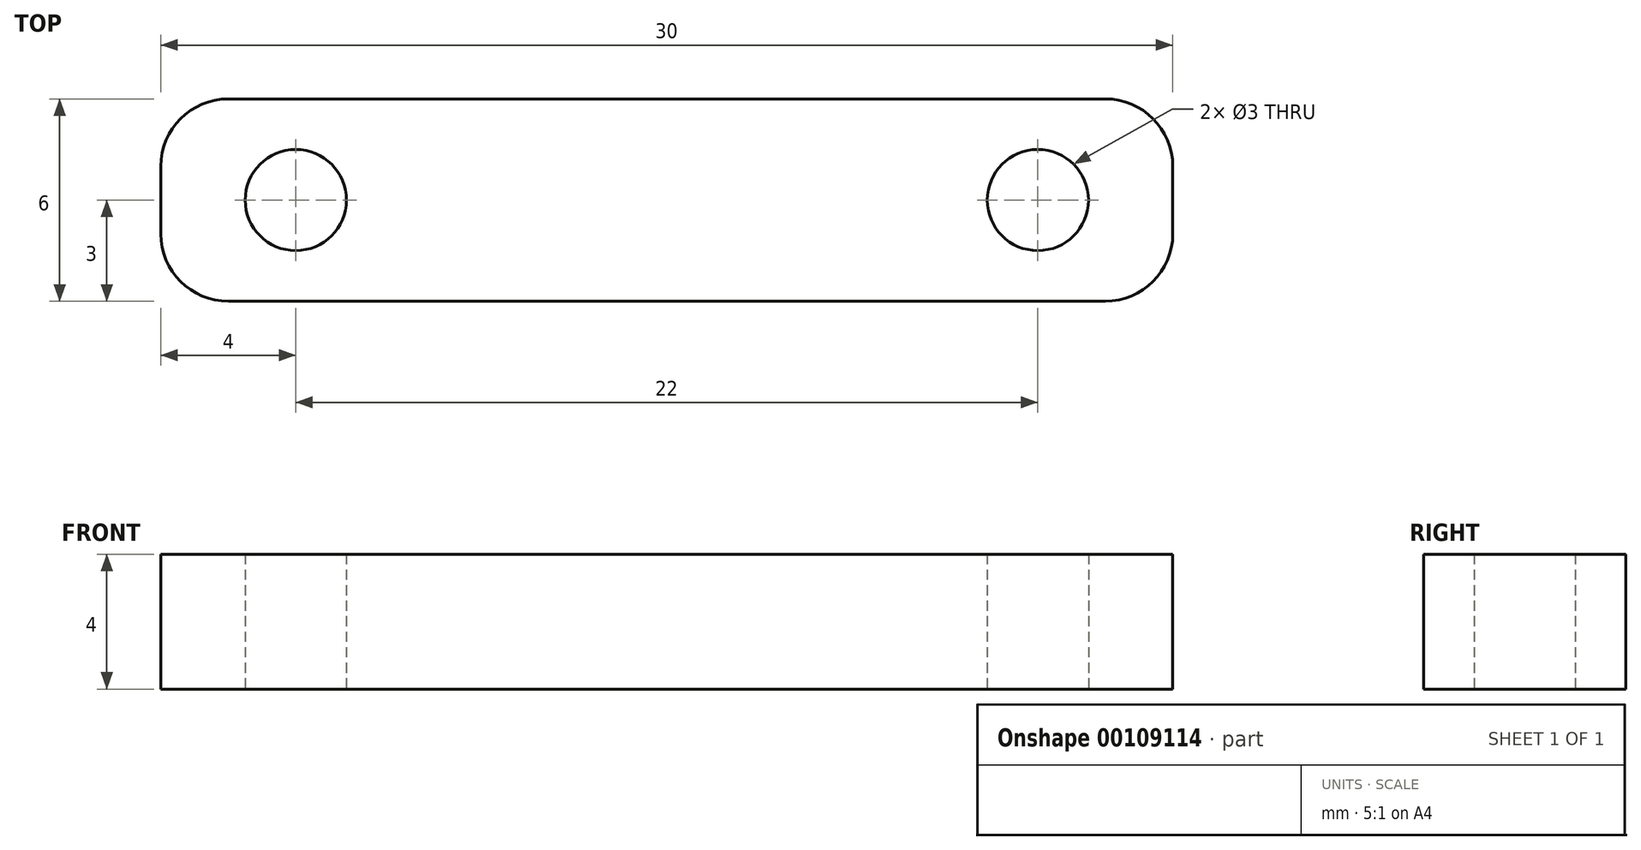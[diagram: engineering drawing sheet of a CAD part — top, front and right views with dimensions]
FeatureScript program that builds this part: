
annotation { "Feature Type Name" : "Feature", "Feature Type Description" : "" }
export const myFeature = defineFeature(function(context is Context, id is Id, definition is map)
    precondition{}
    {
        {
            var Q0;
            Q0=qCreatedBy(makeId("Top.planeOp"),FACE);
            var sketch = newSketch(context, id + "F0", { "sketchPlane" : qUnion([Q0])});
            skLineSegment(sketch, "E0.bottom", {"start": v(15, -3) * mm, "end": v(-15, -3) * mm});
            skLineSegment(sketch, "E0.top", {"start": v(15, 3) * mm, "end": v(-15, 3) * mm});
            skLineSegment(sketch, "E0.left", {"start": v(15, -3) * mm, "end": v(15, 3) * mm});
            skLineSegment(sketch, "E0.right", {"start": v(-15, -3) * mm, "end": v(-15, 3) * mm});
            skPoint(sketch, "E0.middle", {"position": v(0, 0) * mm});
            skCircle(sketch, "E1", {"center": v(-11, 0) * mm, "radius": 1.5 * mm});
            skCircle(sketch, "E2", {"center": v(11, 0) * mm, "radius": 1.5 * mm});
            skSolve(sketch);
        }
        {
            var Q0;
            Q0=makeQuery(id+"F0.imprint","IMPRINT",FACE,{"disambiguationData":[TD([[makeQuery(id+"F0.imprint","IMPRINT",EDGE,{"derivedFrom":sQuery(id+"F0.wireOp",EDGE,"E0.bottom")}),-1.0]])]});
            extrude(context, id + "F1", {"entities" : qUnion([Q0]), "depth" : 4 * mm});
        }
        {
            var Q0;
            Q0=makeQuery(id+"F1.opExtrude","SWEPT_EDGE",EDGE,{"disambiguationData":[OSD([sQuery(id+"F0.wireOp",EDGE,"E0.top"),sQuery(id+"F0.wireOp",EDGE,"E0.right")])]});
            var Q1;
            Q1=makeQuery(id+"F1.opExtrude","SWEPT_EDGE",EDGE,{"disambiguationData":[OSD([sQuery(id+"F0.wireOp",EDGE,"E0.top"),sQuery(id+"F0.wireOp",EDGE,"E0.left")])]});
            var Q2;
            Q2=makeQuery(id+"F1.opExtrude","SWEPT_EDGE",EDGE,{"disambiguationData":[OSD([sQuery(id+"F0.wireOp",EDGE,"E0.bottom"),sQuery(id+"F0.wireOp",EDGE,"E0.left")])]});
            var Q3;
            Q3=makeQuery(id+"F1.opExtrude","SWEPT_EDGE",EDGE,{"disambiguationData":[OSD([sQuery(id+"F0.wireOp",EDGE,"E0.bottom"),sQuery(id+"F0.wireOp",EDGE,"E0.right")])]});
            fillet(context, id + "F2", {"entities" : qUnion([Q0, Q1, Q2, Q3]), "radius" : 2 * mm, "tangentPropagation" : true, "allowEdgeOverflow" : false});
        }
    });
